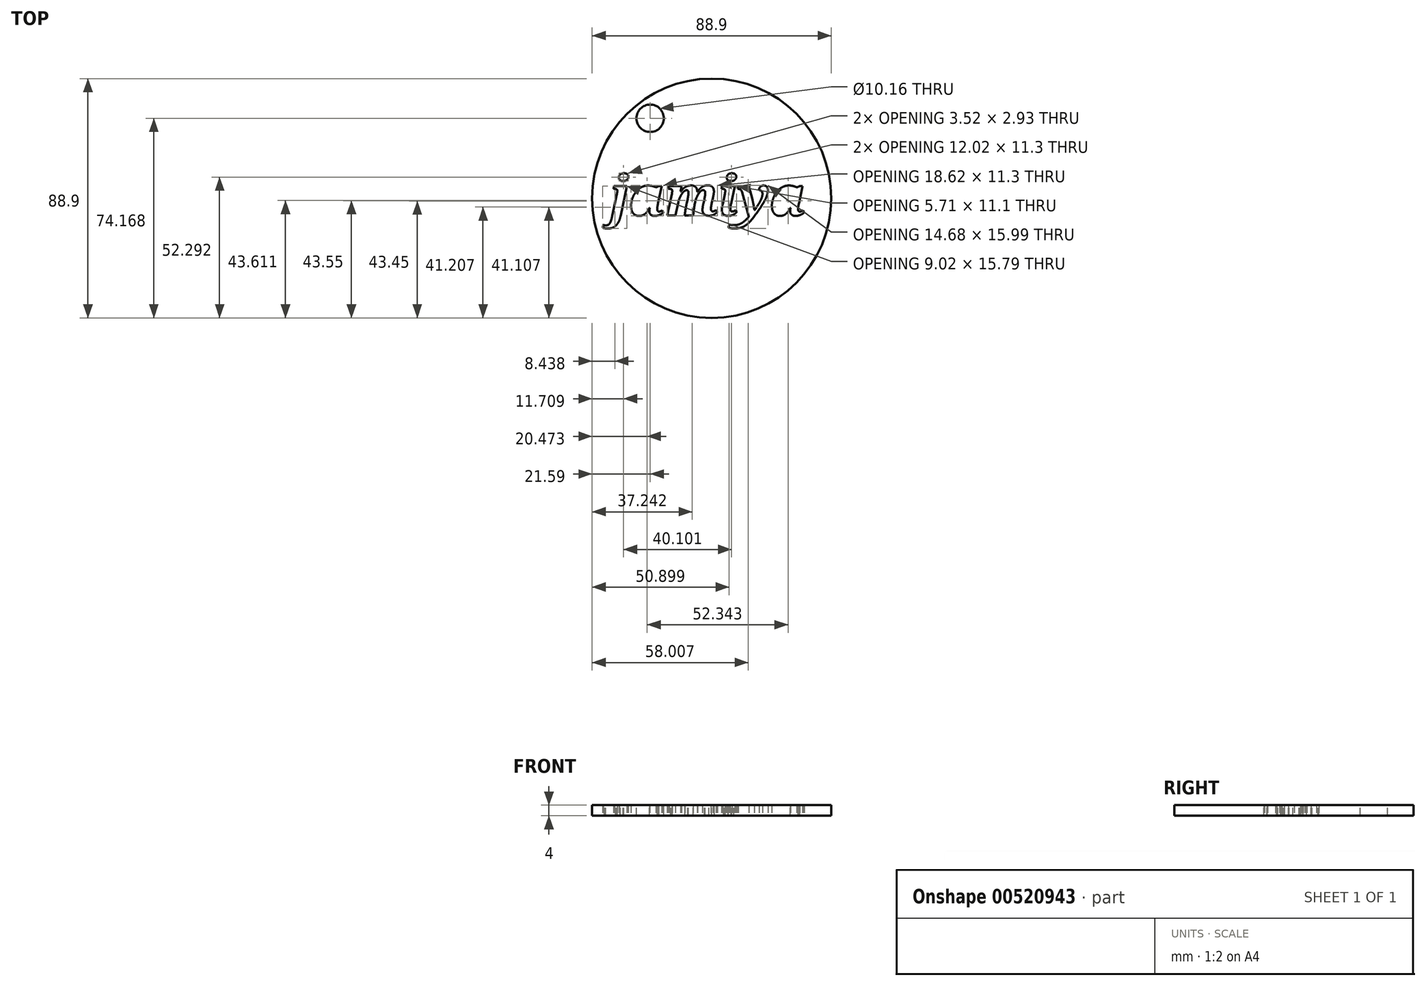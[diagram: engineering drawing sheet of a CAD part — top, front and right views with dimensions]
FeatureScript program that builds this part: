
annotation { "Feature Type Name" : "Feature", "Feature Type Description" : "" }
export const myFeature = defineFeature(function(context is Context, id is Id, definition is map)
    precondition{}
    {
        {
            var Q0;
            Q0=qCreatedBy(makeId("Top.planeOp"),FACE);
            var sketch = newSketch(context, id + "F0", { "sketchPlane" : qUnion([Q0])});
            skCircle(sketch, "E0", {"center": v(0, 0) * mm, "radius": 44.45 * mm});
            skText(sketch, "E1", { "text": "jamiya", "fontName": "NotoSerif-BoldItalic.ttf"});
            const initialGuessF0  = {"E1": [-0.03767, -0.00635, 1, 0, 0.01464]};
            skSetInitialGuess(sketch, initialGuessF0);
            skSolve(sketch);
        }
        {
            var Q0;
            Q0=makeQuery(id+"F0.imprint","IMPRINT",FACE,{"disambiguationData":[TD([[makeQuery(id+"F0.imprint","IMPRINT",EDGE,{"derivedFrom":sQuery(id+"F0.wireOp",EDGE,"E0")}),1.0]])]});
            var Q1;
            Q1 = qSketchRegion(id + "F2", true);
            extrude(context, id + "F1", {"entities" : qUnion([Q0, Q1]), "depth" : 4 * mm, "offsetDistance" : 25.4 * mm});
        }
        {
            var Q0;
            Q0=makeQuery(id+"F1.opExtrude","CAP_FACE",FACE,{"disambiguationData":[OSD([sQuery(id+"F0.wireOp",EDGE,"E0"),sQuery(id+"F0.wireOp",EDGE,"E1.sketch_text.stroke-0"),sQuery(id+"F0.wireOp",EDGE,"E1.sketch_text.stroke-1"),sQuery(id+"F0.wireOp",EDGE,"E1.sketch_text.stroke-2"),sQuery(id+"F0.wireOp",EDGE,"E1.sketch_text.stroke-3"),sQuery(id+"F0.wireOp",EDGE,"E1.sketch_text.stroke-4"),sQuery(id+"F0.wireOp",EDGE,"E1.sketch_text.stroke-5"),sQuery(id+"F0.wireOp",EDGE,"E1.sketch_text.stroke-6"),sQuery(id+"F0.wireOp",EDGE,"E1.sketch_text.stroke-7"),sQuery(id+"F0.wireOp",EDGE,"E1.sketch_text.stroke-8"),sQuery(id+"F0.wireOp",EDGE,"E1.sketch_text.stroke-9"),sQuery(id+"F0.wireOp",EDGE,"E1.sketch_text.stroke-10"),sQuery(id+"F0.wireOp",EDGE,"E1.sketch_text.stroke-11"),sQuery(id+"F0.wireOp",EDGE,"E1.sketch_text.stroke-12"),sQuery(id+"F0.wireOp",EDGE,"E1.sketch_text.stroke-13"),sQuery(id+"F0.wireOp",EDGE,"E1.sketch_text.stroke-14"),sQuery(id+"F0.wireOp",EDGE,"E1.sketch_text.stroke-15"),sQuery(id+"F0.wireOp",EDGE,"E1.sketch_text.stroke-16"),sQuery(id+"F0.wireOp",EDGE,"E1.sketch_text.stroke-17"),sQuery(id+"F0.wireOp",EDGE,"E1.sketch_text.stroke-18"),sQuery(id+"F0.wireOp",EDGE,"E1.sketch_text.stroke-19"),sQuery(id+"F0.wireOp",EDGE,"E1.sketch_text.stroke-20"),sQuery(id+"F0.wireOp",EDGE,"E1.sketch_text.stroke-21"),sQuery(id+"F0.wireOp",EDGE,"E1.sketch_text.stroke-22"),sQuery(id+"F0.wireOp",EDGE,"E1.sketch_text.stroke-23"),sQuery(id+"F0.wireOp",EDGE,"E1.sketch_text.stroke-24"),sQuery(id+"F0.wireOp",EDGE,"E1.sketch_text.stroke-25"),sQuery(id+"F0.wireOp",EDGE,"E1.sketch_text.stroke-26"),sQuery(id+"F0.wireOp",EDGE,"E1.sketch_text.stroke-27"),sQuery(id+"F0.wireOp",EDGE,"E1.sketch_text.stroke-28"),sQuery(id+"F0.wireOp",EDGE,"E1.sketch_text.stroke-29"),sQuery(id+"F0.wireOp",EDGE,"E1.sketch_text.stroke-30"),sQuery(id+"F0.wireOp",EDGE,"E1.sketch_text.stroke-31"),sQuery(id+"F0.wireOp",EDGE,"E1.sketch_text.stroke-32"),sQuery(id+"F0.wireOp",EDGE,"E1.sketch_text.stroke-33"),sQuery(id+"F0.wireOp",EDGE,"E1.sketch_text.stroke-34"),sQuery(id+"F0.wireOp",EDGE,"E1.sketch_text.stroke-35"),sQuery(id+"F0.wireOp",EDGE,"E1.sketch_text.stroke-36"),sQuery(id+"F0.wireOp",EDGE,"E1.sketch_text.stroke-37"),sQuery(id+"F0.wireOp",EDGE,"E1.sketch_text.stroke-38"),sQuery(id+"F0.wireOp",EDGE,"E1.sketch_text.stroke-39"),sQuery(id+"F0.wireOp",EDGE,"E1.sketch_text.stroke-40"),sQuery(id+"F0.wireOp",EDGE,"E1.sketch_text.stroke-41"),sQuery(id+"F0.wireOp",EDGE,"E1.sketch_text.stroke-42"),sQuery(id+"F0.wireOp",EDGE,"E1.sketch_text.stroke-43"),sQuery(id+"F0.wireOp",EDGE,"E1.sketch_text.stroke-44"),sQuery(id+"F0.wireOp",EDGE,"E1.sketch_text.stroke-45"),sQuery(id+"F0.wireOp",EDGE,"E1.sketch_text.stroke-46"),sQuery(id+"F0.wireOp",EDGE,"E1.sketch_text.stroke-47"),sQuery(id+"F0.wireOp",EDGE,"E1.sketch_text.stroke-48"),sQuery(id+"F0.wireOp",EDGE,"E1.sketch_text.stroke-49"),sQuery(id+"F0.wireOp",EDGE,"E1.sketch_text.stroke-50"),sQuery(id+"F0.wireOp",EDGE,"E1.sketch_text.stroke-51"),sQuery(id+"F0.wireOp",EDGE,"E1.sketch_text.stroke-52"),sQuery(id+"F0.wireOp",EDGE,"E1.sketch_text.stroke-53"),sQuery(id+"F0.wireOp",EDGE,"E1.sketch_text.stroke-54"),sQuery(id+"F0.wireOp",EDGE,"E1.sketch_text.stroke-55"),sQuery(id+"F0.wireOp",EDGE,"E1.sketch_text.stroke-56"),sQuery(id+"F0.wireOp",EDGE,"E1.sketch_text.stroke-57"),sQuery(id+"F0.wireOp",EDGE,"E1.sketch_text.stroke-58"),sQuery(id+"F0.wireOp",EDGE,"E1.sketch_text.stroke-59"),sQuery(id+"F0.wireOp",EDGE,"E1.sketch_text.stroke-60"),sQuery(id+"F0.wireOp",EDGE,"E1.sketch_text.stroke-61"),sQuery(id+"F0.wireOp",EDGE,"E1.sketch_text.stroke-62"),sQuery(id+"F0.wireOp",EDGE,"E1.sketch_text.stroke-63"),sQuery(id+"F0.wireOp",EDGE,"E1.sketch_text.stroke-64"),sQuery(id+"F0.wireOp",EDGE,"E1.sketch_text.stroke-65"),sQuery(id+"F0.wireOp",EDGE,"E1.sketch_text.stroke-66"),sQuery(id+"F0.wireOp",EDGE,"E1.sketch_text.stroke-67"),sQuery(id+"F0.wireOp",EDGE,"E1.sketch_text.stroke-68"),sQuery(id+"F0.wireOp",EDGE,"E1.sketch_text.stroke-69"),sQuery(id+"F0.wireOp",EDGE,"E1.sketch_text.stroke-70"),sQuery(id+"F0.wireOp",EDGE,"E1.sketch_text.stroke-71"),sQuery(id+"F0.wireOp",EDGE,"E1.sketch_text.stroke-72"),sQuery(id+"F0.wireOp",EDGE,"E1.sketch_text.stroke-73"),sQuery(id+"F0.wireOp",EDGE,"E1.sketch_text.stroke-74"),sQuery(id+"F0.wireOp",EDGE,"E1.sketch_text.stroke-75"),sQuery(id+"F0.wireOp",EDGE,"E1.sketch_text.stroke-76"),sQuery(id+"F0.wireOp",EDGE,"E1.sketch_text.stroke-77"),sQuery(id+"F0.wireOp",EDGE,"E1.sketch_text.stroke-78"),sQuery(id+"F0.wireOp",EDGE,"E1.sketch_text.stroke-79"),sQuery(id+"F0.wireOp",EDGE,"E1.sketch_text.stroke-80"),sQuery(id+"F0.wireOp",EDGE,"E1.sketch_text.stroke-98"),sQuery(id+"F0.wireOp",EDGE,"E1.sketch_text.stroke-99"),sQuery(id+"F0.wireOp",EDGE,"E1.sketch_text.stroke-100"),sQuery(id+"F0.wireOp",EDGE,"E1.sketch_text.stroke-101"),sQuery(id+"F0.wireOp",EDGE,"E1.sketch_text.stroke-102"),sQuery(id+"F0.wireOp",EDGE,"E1.sketch_text.stroke-103"),sQuery(id+"F0.wireOp",EDGE,"E1.sketch_text.stroke-104"),sQuery(id+"F0.wireOp",EDGE,"E1.sketch_text.stroke-105"),sQuery(id+"F0.wireOp",EDGE,"E1.sketch_text.stroke-106"),sQuery(id+"F0.wireOp",EDGE,"E1.sketch_text.stroke-107"),sQuery(id+"F0.wireOp",EDGE,"E1.sketch_text.stroke-108"),sQuery(id+"F0.wireOp",EDGE,"E1.sketch_text.stroke-109"),sQuery(id+"F0.wireOp",EDGE,"E1.sketch_text.stroke-110"),sQuery(id+"F0.wireOp",EDGE,"E1.sketch_text.stroke-111"),sQuery(id+"F0.wireOp",EDGE,"E1.sketch_text.stroke-112"),sQuery(id+"F0.wireOp",EDGE,"E1.sketch_text.stroke-113"),sQuery(id+"F0.wireOp",EDGE,"E1.sketch_text.stroke-114"),sQuery(id+"F0.wireOp",EDGE,"E1.sketch_text.stroke-115"),sQuery(id+"F0.wireOp",EDGE,"E1.sketch_text.stroke-116"),sQuery(id+"F0.wireOp",EDGE,"E1.sketch_text.stroke-117"),sQuery(id+"F0.wireOp",EDGE,"E1.sketch_text.stroke-118"),sQuery(id+"F0.wireOp",EDGE,"E1.sketch_text.stroke-119"),sQuery(id+"F0.wireOp",EDGE,"E1.sketch_text.stroke-120"),sQuery(id+"F0.wireOp",EDGE,"E1.sketch_text.stroke-121"),sQuery(id+"F0.wireOp",EDGE,"E1.sketch_text.stroke-122"),sQuery(id+"F0.wireOp",EDGE,"E1.sketch_text.stroke-123"),sQuery(id+"F0.wireOp",EDGE,"E1.sketch_text.stroke-124"),sQuery(id+"F0.wireOp",EDGE,"E1.sketch_text.stroke-125"),sQuery(id+"F0.wireOp",EDGE,"E1.sketch_text.stroke-126"),sQuery(id+"F0.wireOp",EDGE,"E1.sketch_text.stroke-127"),sQuery(id+"F0.wireOp",EDGE,"E1.sketch_text.stroke-128"),sQuery(id+"F0.wireOp",EDGE,"E1.sketch_text.stroke-129"),sQuery(id+"F0.wireOp",EDGE,"E1.sketch_text.stroke-130"),sQuery(id+"F0.wireOp",EDGE,"E1.sketch_text.stroke-131"),sQuery(id+"F0.wireOp",EDGE,"E1.sketch_text.stroke-132"),sQuery(id+"F0.wireOp",EDGE,"E1.sketch_text.stroke-133"),sQuery(id+"F0.wireOp",EDGE,"E1.sketch_text.stroke-134"),sQuery(id+"F0.wireOp",EDGE,"E1.sketch_text.stroke-135"),sQuery(id+"F0.wireOp",EDGE,"E1.sketch_text.stroke-136"),sQuery(id+"F0.wireOp",EDGE,"E1.sketch_text.stroke-137"),sQuery(id+"F0.wireOp",EDGE,"E1.sketch_text.stroke-138"),sQuery(id+"F0.wireOp",EDGE,"E1.sketch_text.stroke-139"),sQuery(id+"F0.wireOp",EDGE,"E1.sketch_text.stroke-140"),sQuery(id+"F0.wireOp",EDGE,"E1.sketch_text.stroke-141"),sQuery(id+"F0.wireOp",EDGE,"E1.sketch_text.stroke-142"),sQuery(id+"F0.wireOp",EDGE,"E1.sketch_text.stroke-143"),sQuery(id+"F0.wireOp",EDGE,"E1.sketch_text.stroke-144"),sQuery(id+"F0.wireOp",EDGE,"E1.sketch_text.stroke-145"),sQuery(id+"F0.wireOp",EDGE,"E1.sketch_text.stroke-146"),sQuery(id+"F0.wireOp",EDGE,"E1.sketch_text.stroke-147"),sQuery(id+"F0.wireOp",EDGE,"E1.sketch_text.stroke-148"),sQuery(id+"F0.wireOp",EDGE,"E1.sketch_text.stroke-149"),sQuery(id+"F0.wireOp",EDGE,"E1.sketch_text.stroke-150"),sQuery(id+"F0.wireOp",EDGE,"E1.sketch_text.stroke-151"),sQuery(id+"F0.wireOp",EDGE,"E1.sketch_text.stroke-152"),sQuery(id+"F0.wireOp",EDGE,"E1.sketch_text.stroke-153"),sQuery(id+"F0.wireOp",EDGE,"E1.sketch_text.stroke-154"),sQuery(id+"F0.wireOp",EDGE,"E1.sketch_text.stroke-155"),sQuery(id+"F0.wireOp",EDGE,"E1.sketch_text.stroke-156"),sQuery(id+"F0.wireOp",EDGE,"E1.sketch_text.stroke-157"),sQuery(id+"F0.wireOp",EDGE,"E1.sketch_text.stroke-158"),sQuery(id+"F0.wireOp",EDGE,"E1.sketch_text.stroke-159"),sQuery(id+"F0.wireOp",EDGE,"E1.sketch_text.stroke-160"),sQuery(id+"F0.wireOp",EDGE,"E1.sketch_text.stroke-161"),sQuery(id+"F0.wireOp",EDGE,"E1.sketch_text.stroke-162"),sQuery(id+"F0.wireOp",EDGE,"E1.sketch_text.stroke-163"),sQuery(id+"F0.wireOp",EDGE,"E1.sketch_text.stroke-164"),sQuery(id+"F0.wireOp",EDGE,"E1.sketch_text.stroke-165"),sQuery(id+"F0.wireOp",EDGE,"E1.sketch_text.stroke-166"),sQuery(id+"F0.wireOp",EDGE,"E1.sketch_text.stroke-167"),sQuery(id+"F0.wireOp",EDGE,"E1.sketch_text.stroke-168"),sQuery(id+"F0.wireOp",EDGE,"E1.sketch_text.stroke-169"),sQuery(id+"F0.wireOp",EDGE,"E1.sketch_text.stroke-170"),sQuery(id+"F0.wireOp",EDGE,"E1.sketch_text.stroke-171"),sQuery(id+"F0.wireOp",EDGE,"E1.sketch_text.stroke-172"),sQuery(id+"F0.wireOp",EDGE,"E1.sketch_text.stroke-173"),sQuery(id+"F0.wireOp",EDGE,"E1.sketch_text.stroke-174"),sQuery(id+"F0.wireOp",EDGE,"E1.sketch_text.stroke-175"),sQuery(id+"F0.wireOp",EDGE,"E1.sketch_text.stroke-176"),sQuery(id+"F0.wireOp",EDGE,"E1.sketch_text.stroke-177"),sQuery(id+"F0.wireOp",EDGE,"E1.sketch_text.stroke-178"),sQuery(id+"F0.wireOp",EDGE,"E1.sketch_text.stroke-179"),sQuery(id+"F0.wireOp",EDGE,"E1.sketch_text.stroke-180"),sQuery(id+"F0.wireOp",EDGE,"E1.sketch_text.stroke-181"),sQuery(id+"F0.wireOp",EDGE,"E1.sketch_text.stroke-182"),sQuery(id+"F0.wireOp",EDGE,"E1.sketch_text.stroke-183"),sQuery(id+"F0.wireOp",EDGE,"E1.sketch_text.stroke-184"),sQuery(id+"F0.wireOp",EDGE,"E1.sketch_text.stroke-185"),sQuery(id+"F0.wireOp",EDGE,"E1.sketch_text.stroke-186"),sQuery(id+"F0.wireOp",EDGE,"E1.sketch_text.stroke-187"),sQuery(id+"F0.wireOp",EDGE,"E1.sketch_text.stroke-188"),sQuery(id+"F0.wireOp",EDGE,"E1.sketch_text.stroke-189"),sQuery(id+"F0.wireOp",EDGE,"E1.sketch_text.stroke-190"),sQuery(id+"F0.wireOp",EDGE,"E1.sketch_text.stroke-191"),sQuery(id+"F0.wireOp",EDGE,"E1.sketch_text.stroke-192"),sQuery(id+"F0.wireOp",EDGE,"E1.sketch_text.stroke-193"),sQuery(id+"F0.wireOp",EDGE,"E1.sketch_text.stroke-194"),sQuery(id+"F0.wireOp",EDGE,"E1.sketch_text.stroke-195"),sQuery(id+"F0.wireOp",EDGE,"E1.sketch_text.stroke-196"),sQuery(id+"F0.wireOp",EDGE,"E1.sketch_text.stroke-197"),sQuery(id+"F0.wireOp",EDGE,"E1.sketch_text.stroke-198"),sQuery(id+"F0.wireOp",EDGE,"E1.sketch_text.stroke-199"),sQuery(id+"F0.wireOp",EDGE,"E1.sketch_text.stroke-200"),sQuery(id+"F0.wireOp",EDGE,"E1.sketch_text.stroke-201"),sQuery(id+"F0.wireOp",EDGE,"E1.sketch_text.stroke-202"),sQuery(id+"F0.wireOp",EDGE,"E1.sketch_text.stroke-203"),sQuery(id+"F0.wireOp",EDGE,"E1.sketch_text.stroke-204"),sQuery(id+"F0.wireOp",EDGE,"E1.sketch_text.stroke-205"),sQuery(id+"F0.wireOp",EDGE,"E1.sketch_text.stroke-206"),sQuery(id+"F0.wireOp",EDGE,"E1.sketch_text.stroke-207"),sQuery(id+"F0.wireOp",EDGE,"E1.sketch_text.stroke-208"),sQuery(id+"F0.wireOp",EDGE,"E1.sketch_text.stroke-209"),sQuery(id+"F0.wireOp",EDGE,"E1.sketch_text.stroke-210"),sQuery(id+"F0.wireOp",EDGE,"E1.sketch_text.stroke-211"),sQuery(id+"F0.wireOp",EDGE,"E1.sketch_text.stroke-212"),sQuery(id+"F0.wireOp",EDGE,"E1.sketch_text.stroke-213"),sQuery(id+"F0.wireOp",EDGE,"E1.sketch_text.stroke-214"),sQuery(id+"F0.wireOp",EDGE,"E1.sketch_text.stroke-215"),sQuery(id+"F0.wireOp",EDGE,"E1.sketch_text.stroke-216"),sQuery(id+"F0.wireOp",EDGE,"E1.sketch_text.stroke-217"),sQuery(id+"F0.wireOp",EDGE,"E1.sketch_text.stroke-218"),sQuery(id+"F0.wireOp",EDGE,"E1.sketch_text.stroke-219"),sQuery(id+"F0.wireOp",EDGE,"E1.sketch_text.stroke-220"),sQuery(id+"F0.wireOp",EDGE,"E1.sketch_text.stroke-221"),sQuery(id+"F0.wireOp",EDGE,"E1.sketch_text.stroke-222"),sQuery(id+"F0.wireOp",EDGE,"E1.sketch_text.stroke-223"),sQuery(id+"F0.wireOp",EDGE,"E1.sketch_text.stroke-224"),sQuery(id+"F0.wireOp",EDGE,"E1.sketch_text.stroke-225"),sQuery(id+"F0.wireOp",EDGE,"E1.sketch_text.stroke-226"),sQuery(id+"F0.wireOp",EDGE,"E1.sketch_text.stroke-227"),sQuery(id+"F0.wireOp",EDGE,"E1.sketch_text.stroke-228"),sQuery(id+"F0.wireOp",EDGE,"E1.sketch_text.stroke-229"),sQuery(id+"F0.wireOp",EDGE,"E1.sketch_text.stroke-230"),sQuery(id+"F0.wireOp",EDGE,"E1.sketch_text.stroke-231"),sQuery(id+"F0.wireOp",EDGE,"E1.sketch_text.stroke-232"),sQuery(id+"F0.wireOp",EDGE,"E1.sketch_text.stroke-233"),sQuery(id+"F0.wireOp",EDGE,"E1.sketch_text.stroke-234"),sQuery(id+"F0.wireOp",EDGE,"E1.sketch_text.stroke-235"),sQuery(id+"F0.wireOp",EDGE,"E1.sketch_text.stroke-236"),sQuery(id+"F0.wireOp",EDGE,"E1.sketch_text.stroke-237"),sQuery(id+"F0.wireOp",EDGE,"E1.sketch_text.stroke-238"),sQuery(id+"F0.wireOp",EDGE,"E1.sketch_text.stroke-239"),sQuery(id+"F0.wireOp",EDGE,"E1.sketch_text.stroke-240"),sQuery(id+"F0.wireOp",EDGE,"E1.sketch_text.stroke-241"),sQuery(id+"F0.wireOp",EDGE,"E1.sketch_text.stroke-242"),sQuery(id+"F0.wireOp",EDGE,"E1.sketch_text.stroke-243"),sQuery(id+"F0.wireOp",EDGE,"E1.sketch_text.stroke-244"),sQuery(id+"F0.wireOp",EDGE,"E1.sketch_text.stroke-245"),sQuery(id+"F0.wireOp",EDGE,"E1.sketch_text.stroke-246"),sQuery(id+"F0.wireOp",EDGE,"E1.sketch_text.stroke-247"),sQuery(id+"F0.wireOp",EDGE,"E1.sketch_text.stroke-248"),sQuery(id+"F0.wireOp",EDGE,"E1.sketch_text.stroke-249"),sQuery(id+"F0.wireOp",EDGE,"E1.sketch_text.stroke-250"),sQuery(id+"F0.wireOp",EDGE,"E1.sketch_text.stroke-251"),sQuery(id+"F0.wireOp",EDGE,"E1.sketch_text.stroke-252"),sQuery(id+"F0.wireOp",EDGE,"E1.sketch_text.stroke-253"),sQuery(id+"F0.wireOp",EDGE,"E1.sketch_text.stroke-254"),sQuery(id+"F0.wireOp",EDGE,"E1.sketch_text.stroke-255"),sQuery(id+"F0.wireOp",EDGE,"E1.sketch_text.stroke-256"),sQuery(id+"F0.wireOp",EDGE,"E1.sketch_text.stroke-257"),sQuery(id+"F0.wireOp",EDGE,"E1.sketch_text.stroke-258"),sQuery(id+"F0.wireOp",EDGE,"E1.sketch_text.stroke-259"),sQuery(id+"F0.wireOp",EDGE,"E1.sketch_text.stroke-260"),sQuery(id+"F0.wireOp",EDGE,"E1.sketch_text.stroke-261"),sQuery(id+"F0.wireOp",EDGE,"E1.sketch_text.stroke-262"),sQuery(id+"F0.wireOp",EDGE,"E1.sketch_text.stroke-263"),sQuery(id+"F0.wireOp",EDGE,"E1.sketch_text.stroke-264"),sQuery(id+"F0.wireOp",EDGE,"E1.sketch_text.stroke-265"),sQuery(id+"F0.wireOp",EDGE,"E1.sketch_text.stroke-266"),sQuery(id+"F0.wireOp",EDGE,"E1.sketch_text.stroke-267"),sQuery(id+"F0.wireOp",EDGE,"E1.sketch_text.stroke-268"),sQuery(id+"F0.wireOp",EDGE,"E1.sketch_text.stroke-269"),sQuery(id+"F0.wireOp",EDGE,"E1.sketch_text.stroke-270"),sQuery(id+"F0.wireOp",EDGE,"E1.sketch_text.stroke-271"),sQuery(id+"F0.wireOp",EDGE,"E1.sketch_text.stroke-272"),sQuery(id+"F0.wireOp",EDGE,"E1.sketch_text.stroke-273"),sQuery(id+"F0.wireOp",EDGE,"E1.sketch_text.stroke-274"),sQuery(id+"F0.wireOp",EDGE,"E1.sketch_text.stroke-275"),sQuery(id+"F0.wireOp",EDGE,"E1.sketch_text.stroke-276"),sQuery(id+"F0.wireOp",EDGE,"E1.sketch_text.stroke-277"),sQuery(id+"F0.wireOp",EDGE,"E1.sketch_text.stroke-278"),sQuery(id+"F0.wireOp",EDGE,"E1.sketch_text.stroke-279"),sQuery(id+"F0.wireOp",EDGE,"E1.sketch_text.stroke-280"),sQuery(id+"F0.wireOp",EDGE,"E1.sketch_text.stroke-281"),sQuery(id+"F0.wireOp",EDGE,"E1.sketch_text.stroke-282"),sQuery(id+"F0.wireOp",EDGE,"E1.sketch_text.stroke-283"),sQuery(id+"F0.wireOp",EDGE,"E1.sketch_text.stroke-284"),sQuery(id+"F0.wireOp",EDGE,"E1.sketch_text.stroke-285"),sQuery(id+"F0.wireOp",EDGE,"E1.sketch_text.stroke-286"),sQuery(id+"F0.wireOp",EDGE,"E1.sketch_text.stroke-287"),sQuery(id+"F0.wireOp",EDGE,"E1.sketch_text.stroke-288"),sQuery(id+"F0.wireOp",EDGE,"E1.sketch_text.stroke-289"),sQuery(id+"F0.wireOp",EDGE,"E1.sketch_text.stroke-290"),sQuery(id+"F0.wireOp",EDGE,"E1.sketch_text.stroke-291"),sQuery(id+"F0.wireOp",EDGE,"E1.sketch_text.stroke-292"),sQuery(id+"F0.wireOp",EDGE,"E1.sketch_text.stroke-293"),sQuery(id+"F0.wireOp",EDGE,"E1.sketch_text.stroke-294"),sQuery(id+"F0.wireOp",EDGE,"E1.sketch_text.stroke-295"),sQuery(id+"F0.wireOp",EDGE,"E1.sketch_text.stroke-296"),sQuery(id+"F0.wireOp",EDGE,"E1.sketch_text.stroke-297"),sQuery(id+"F0.wireOp",EDGE,"E1.sketch_text.stroke-298"),sQuery(id+"F0.wireOp",EDGE,"E1.sketch_text.stroke-299"),sQuery(id+"F0.wireOp",EDGE,"E1.sketch_text.stroke-300"),sQuery(id+"F0.wireOp",EDGE,"E1.sketch_text.stroke-301"),sQuery(id+"F0.wireOp",EDGE,"E1.sketch_text.stroke-302"),sQuery(id+"F0.wireOp",EDGE,"E1.sketch_text.stroke-303"),sQuery(id+"F0.wireOp",EDGE,"E1.sketch_text.stroke-304"),sQuery(id+"F0.wireOp",EDGE,"E1.sketch_text.stroke-305"),sQuery(id+"F0.wireOp",EDGE,"E1.sketch_text.stroke-306"),sQuery(id+"F0.wireOp",EDGE,"E1.sketch_text.stroke-307"),sQuery(id+"F0.wireOp",EDGE,"E1.sketch_text.stroke-308"),sQuery(id+"F0.wireOp",EDGE,"E1.sketch_text.stroke-309"),sQuery(id+"F0.wireOp",EDGE,"E1.sketch_text.stroke-310"),sQuery(id+"F0.wireOp",EDGE,"E1.sketch_text.stroke-311"),sQuery(id+"F0.wireOp",EDGE,"E1.sketch_text.stroke-312"),sQuery(id+"F0.wireOp",EDGE,"E1.sketch_text.stroke-313"),sQuery(id+"F0.wireOp",EDGE,"E1.sketch_text.stroke-314"),sQuery(id+"F0.wireOp",EDGE,"E1.sketch_text.stroke-315"),sQuery(id+"F0.wireOp",EDGE,"E1.sketch_text.stroke-316"),sQuery(id+"F0.wireOp",EDGE,"E1.sketch_text.stroke-317"),sQuery(id+"F0.wireOp",EDGE,"E1.sketch_text.stroke-318"),sQuery(id+"F0.wireOp",EDGE,"E1.sketch_text.stroke-319"),sQuery(id+"F0.wireOp",EDGE,"E1.sketch_text.stroke-320"),sQuery(id+"F0.wireOp",EDGE,"E1.sketch_text.stroke-321")])],"isStart":false});
            var sketch = newSketch(context, id + "F2", { "sketchPlane" : qUnion([Q0])});
            skCircle(sketch, "E2", {"center": v(-22.86, 29.72) * mm, "radius": 5.08 * mm});
            skSolve(sketch);
        }
        {
            var Q0;
            Q0=makeQuery(id+"F2.imprint","IMPRINT",FACE,{"disambiguationData":[TD([[makeQuery(id+"F2.imprint","IMPRINT",EDGE,{"derivedFrom":sQuery(id+"F2.wireOp",EDGE,"E2")}),1.0]])]});
            extrude(context, id + "F3", {"entities" : qUnion([Q0]), "operationType" : NewBodyOperationType.REMOVE, "oppositeDirection" : true, "depth" : 25.4 * mm, "offsetDistance" : 25.4 * mm});
        }
    });
